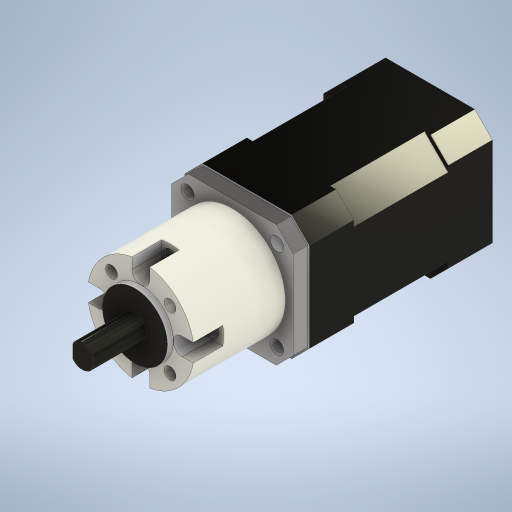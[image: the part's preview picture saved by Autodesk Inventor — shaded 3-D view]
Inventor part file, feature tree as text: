
AUTODESK INVENTOR PART (.ipt)
format: ipt  version: 2024 (Build 280153000, 153)  size: 480,768 bytes
history: native  units: mm
features: extrude x13, sketch x2, chamfer x1, direct_edit x1, other x1
ambient origin geometry x8: Origin, YZ Plane, XZ Plane, XY Plane, X Axis, Y Axis, Z Axis, Center Point
bodies: Solid1 (feature_tree)
feature tree (18):
  extrude  "Extrusion1"  Depth=42.2mm
  extrude  "Extrusion2"  Depth=10.0mm
  extrude  "Extrusion3"  Depth=10.0mm
  extrude  "Extrusion4"  Depth=10.0mm
  extrude  "Extrusion5"  Depth=10.0mm
  extrude  "Extrusion6"  Depth=10.0mm
  sketch  "Sketch7"  dims[d0=42.2mm d1=42.2mm]
  extrude  "Extrusion7"  Depth=10.0mm
  extrude  "Extrusion8"  Depth=10.0mm
  extrude  "Extrusion9"  Depth=10.0mm TaperAngle=0.0deg
  extrude  "Extrusion10"  Depth=10.0mm
  extrude  "Extrusion11"  Depth=10.0mm
  extrude  "Extrusion12"  Depth=10.0mm
  chamfer  "Chamfer1"  Distance=8.0mm
  extrude  "Extrusion13"  Depth=10.0mm
  direct_edit  "Direct Edit1"
  sketch  "Sketch11"  dims[d2=6.0mm d3=6.0mm d4=6.0mm d5=6.0mm d6=6.0mm d7=6.0mm d8=6.0mm d9=6.0mm d10=15.0mm d11=0.0mm d12=42.2mm d13=42.2mm d14=8.0mm d15=8.0mm d16=8.0mm d17=8.0mm d18=8.0mm d19=8.0mm d20=8.0mm d21=8.0mm d22=32.0mm d23=0.0mm d24=42.2mm d25=42.2mm d26=6.0mm d27=6.0mm d28=6.0mm d29=6.0mm d30=6.0mm d31=6.0mm d32=6.0mm d33=6.0mm d34=15.0mm d35=0.0mm d36=0.5mm d37=5.0mm d38=0.0mm d39=36.0mm d40=21.0mm d41=0.0mm d42=36.0mm d43=10.0mm d44=0.0mm d45=5.0mm d46=14.0mm d47=6.0mm d48=40.0mm d50=360.0deg d52=4.0mm d53=80.0mm d55=360.0deg d57=10.0mm d58=0.0mm d59=12.0mm d60=0.0mm d61=6.0mm d62=0.0mm d63=22.0mm d64=2.0mm d65=0.0mm d66=8.0mm d67=18.0mm d68=0.0mm d69=3.0mm d70=15.0mm d71=0.0mm d72=0.25mm d73=2.0mm d74=45.0deg d76=45.0deg d77=4.5mm d78=40.0mm d80=360.0deg d82=5.0mm d83=0.0mm d84=1000.0mm d85=10.0mm d86=10.0mm]
  other  "Scale1"
